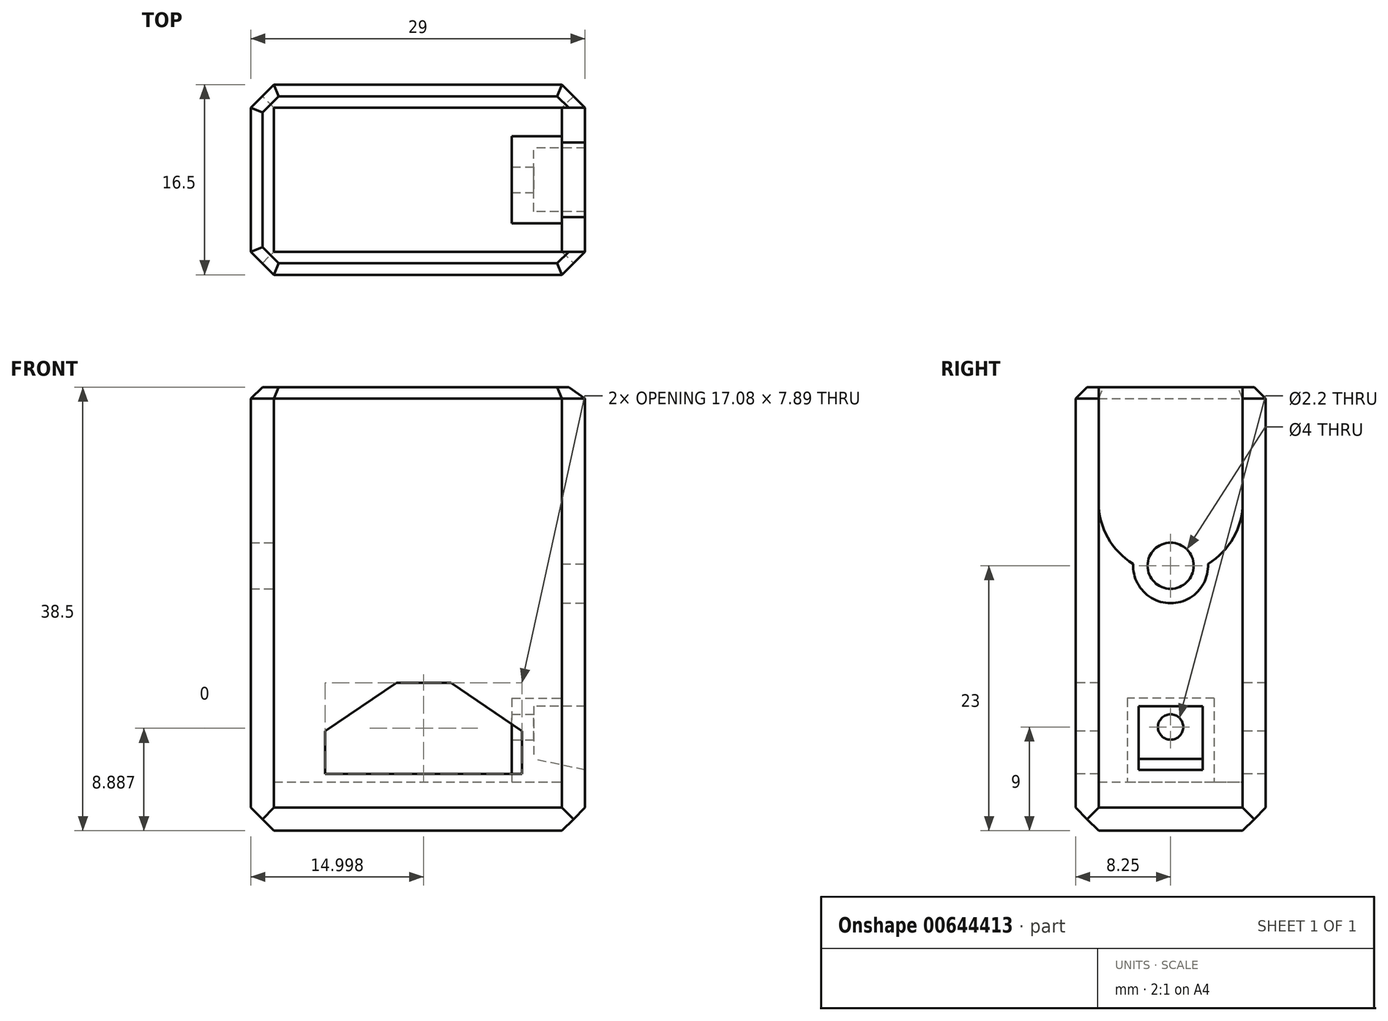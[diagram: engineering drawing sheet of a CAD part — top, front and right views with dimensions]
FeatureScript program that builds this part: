
annotation { "Feature Type Name" : "Feature", "Feature Type Description" : "" }
export const myFeature = defineFeature(function(context is Context, id is Id, definition is map)
    precondition{}
    {
        {
            var Q0;
            Q0=qCreatedBy(makeId("Top.planeOp"),FACE);
            var sketch = newSketch(context, id + "F0", { "sketchPlane" : qUnion([Q0])});
            skLineSegment(sketch, "E0.bottom", {"start": v(0, 0) * mm, "end": v(29, 0) * mm});
            skLineSegment(sketch, "E0.top", {"start": v(0, 16.5) * mm, "end": v(29, 16.5) * mm});
            skLineSegment(sketch, "E0.left", {"start": v(0, 0) * mm, "end": v(0, 16.5) * mm});
            skLineSegment(sketch, "E0.right", {"start": v(29, 0) * mm, "end": v(29, 16.5) * mm});
            skSolve(sketch);
        }
        {
            var Q0;
            Q0 = qSketchRegion(id + "F0", true);
            extrude(context, id + "F1", {"entities" : qUnion([Q0]), "depth" : 38.5 * mm, "offsetDistance" : 25 * mm});
        }
        {
            var Q0;
            Q0=makeQuery(id+"F1.opExtrude","CAP_FACE",FACE,{"disambiguationData":[OSD([sQuery(id+"F0.wireOp",EDGE,"E0.bottom"),sQuery(id+"F0.wireOp",EDGE,"E0.top"),sQuery(id+"F0.wireOp",EDGE,"E0.left"),sQuery(id+"F0.wireOp",EDGE,"E0.right")])],"isStart":false});
            shell(context, id + "F2", {"entities" : qUnion([Q0]), "thickness" : 2 * mm});
        }
        {
            var Q0;
            Q0=makeQuery(id+"F2.opShell","OFFSET_FACE",FACE,{"disambiguationData":[OSD([sQuery(id+"F0.wireOp",EDGE,"E0.bottom"),sQuery(id+"F0.wireOp",EDGE,"E0.top"),sQuery(id+"F0.wireOp",EDGE,"E0.left"),sQuery(id+"F0.wireOp",EDGE,"E0.right")])]});
            extrude(context, id + "F3", {"entities" : qUnion([Q0]), "operationType" : NewBodyOperationType.ADD, "depth" : 2.25 * mm, "offsetDistance" : 25 * mm});
        }
        {
            var Q0;
            Q0=makeQuery(id+"F1.opExtrude","SWEPT_EDGE",EDGE,{"disambiguationData":[OSD([sQuery(id+"F0.wireOp",EDGE,"E0.top"),sQuery(id+"F0.wireOp",EDGE,"E0.right")])]});
            var Q1;
            Q1=makeQuery(id+"F1.opExtrude","SWEPT_EDGE",EDGE,{"disambiguationData":[OSD([sQuery(id+"F0.wireOp",EDGE,"E0.top"),sQuery(id+"F0.wireOp",EDGE,"E0.left")])]});
            var Q2;
            Q2=makeQuery(id+"F1.opExtrude","SWEPT_EDGE",EDGE,{"disambiguationData":[OSD([sQuery(id+"F0.wireOp",EDGE,"E0.bottom"),sQuery(id+"F0.wireOp",EDGE,"E0.left")])]});
            var Q3;
            Q3=makeQuery(id+"F1.opExtrude","SWEPT_EDGE",EDGE,{"disambiguationData":[OSD([sQuery(id+"F0.wireOp",EDGE,"E0.bottom"),sQuery(id+"F0.wireOp",EDGE,"E0.right")])]});
            chamfer(context, id + "F4", {"entities" : qUnion([Q0, Q1, Q2, Q3]), "width" : 2 * mm, "tangentPropagation" : true});
        }
        {
            var Q0;
            Q0=makeQuery(id+"F1.opExtrude","CAP_EDGE",EDGE,{"disambiguationData":[OSD([sQuery(id+"F0.wireOp",EDGE,"E0.left")])],"isStart":true});
            var Q1;
            Q1=makeQuery(id+"F1.opExtrude","CAP_EDGE",EDGE,{"disambiguationData":[OSD([sQuery(id+"F0.wireOp",EDGE,"E0.bottom")])],"isStart":true});
            var Q2;
            Q2=makeQuery(id+"F1.opExtrude","CAP_EDGE",EDGE,{"disambiguationData":[OSD([sQuery(id+"F0.wireOp",EDGE,"E0.right")])],"isStart":true});
            var Q3;
            Q3=makeQuery(id+"F1.opExtrude","CAP_EDGE",EDGE,{"disambiguationData":[OSD([sQuery(id+"F0.wireOp",EDGE,"E0.top")])],"isStart":true});
            chamfer(context, id + "F5", {"entities" : qUnion([Q0, Q1, Q2, Q3]), "width" : 2 * mm, "tangentPropagation" : true});
        }
        {
            var Q0;
            Q0=makeQuery(id+"F1.opExtrude","CAP_EDGE",EDGE,{"disambiguationData":[OSD([sQuery(id+"F0.wireOp",EDGE,"E0.top")])],"isStart":false});
            var Q1;
            Q1=makeQuery(id+"F1.opExtrude","CAP_EDGE",EDGE,{"disambiguationData":[OSD([sQuery(id+"F0.wireOp",EDGE,"E0.right")])],"isStart":false});
            var Q2;
            Q2=makeQuery(id+"F1.opExtrude","CAP_EDGE",EDGE,{"disambiguationData":[OSD([sQuery(id+"F0.wireOp",EDGE,"E0.bottom")])],"isStart":false});
            var Q3;
            Q3=makeQuery(id+"F1.opExtrude","CAP_EDGE",EDGE,{"disambiguationData":[OSD([sQuery(id+"F0.wireOp",EDGE,"E0.left")])],"isStart":false});
            var Q4;
            {var subQ0=sQuery(id+"F0.wireOp",EDGE,"E0.left");var subQ1=sQuery(id+"F0.wireOp",EDGE,"E0.top");Q4=makeQuery(id+"F4.opChamfer","BLEND_EDGE",EDGE,{"blendedFrom":[makeQuery(id+"F1.opExtrude","SWEPT_EDGE",EDGE,{"disambiguationData":[OSD([subQ1,subQ0])]}),makeQuery(id+"F1.opExtrude","CAP_FACE",FACE,{"disambiguationData":[OSD([sQuery(id+"F0.wireOp",EDGE,"E0.bottom"),subQ1,subQ0,sQuery(id+"F0.wireOp",EDGE,"E0.right")])],"isStart":false})],"blendedInto":[makeQuery(id+"F1.opExtrude","CAP_FACE",FACE,{"disambiguationData":[OSD([sQuery(id+"F0.wireOp",EDGE,"E0.bottom"),subQ1,subQ0,sQuery(id+"F0.wireOp",EDGE,"E0.right")])],"isStart":false})]});}
            var Q5;
            {var subQ0=sQuery(id+"F0.wireOp",EDGE,"E0.right");var subQ1=sQuery(id+"F0.wireOp",EDGE,"E0.top");Q5=makeQuery(id+"F4.opChamfer","BLEND_EDGE",EDGE,{"blendedFrom":[makeQuery(id+"F1.opExtrude","SWEPT_EDGE",EDGE,{"disambiguationData":[OSD([subQ1,subQ0])]}),makeQuery(id+"F1.opExtrude","CAP_FACE",FACE,{"disambiguationData":[OSD([sQuery(id+"F0.wireOp",EDGE,"E0.bottom"),subQ1,sQuery(id+"F0.wireOp",EDGE,"E0.left"),subQ0])],"isStart":false})],"blendedInto":[makeQuery(id+"F1.opExtrude","CAP_FACE",FACE,{"disambiguationData":[OSD([sQuery(id+"F0.wireOp",EDGE,"E0.bottom"),subQ1,sQuery(id+"F0.wireOp",EDGE,"E0.left"),subQ0])],"isStart":false})]});}
            var Q6;
            {var subQ0=sQuery(id+"F0.wireOp",EDGE,"E0.right");var subQ1=sQuery(id+"F0.wireOp",EDGE,"E0.bottom");Q6=makeQuery(id+"F4.opChamfer","BLEND_EDGE",EDGE,{"blendedFrom":[makeQuery(id+"F1.opExtrude","SWEPT_EDGE",EDGE,{"disambiguationData":[OSD([subQ1,subQ0])]}),makeQuery(id+"F1.opExtrude","CAP_FACE",FACE,{"disambiguationData":[OSD([subQ1,sQuery(id+"F0.wireOp",EDGE,"E0.top"),sQuery(id+"F0.wireOp",EDGE,"E0.left"),subQ0])],"isStart":false})],"blendedInto":[makeQuery(id+"F1.opExtrude","CAP_FACE",FACE,{"disambiguationData":[OSD([subQ1,sQuery(id+"F0.wireOp",EDGE,"E0.top"),sQuery(id+"F0.wireOp",EDGE,"E0.left"),subQ0])],"isStart":false})]});}
            var Q7;
            {var subQ0=sQuery(id+"F0.wireOp",EDGE,"E0.left");var subQ1=sQuery(id+"F0.wireOp",EDGE,"E0.bottom");Q7=makeQuery(id+"F4.opChamfer","BLEND_EDGE",EDGE,{"blendedFrom":[makeQuery(id+"F1.opExtrude","SWEPT_EDGE",EDGE,{"disambiguationData":[OSD([subQ1,subQ0])]}),makeQuery(id+"F1.opExtrude","CAP_FACE",FACE,{"disambiguationData":[OSD([subQ1,sQuery(id+"F0.wireOp",EDGE,"E0.top"),subQ0,sQuery(id+"F0.wireOp",EDGE,"E0.right")])],"isStart":false})],"blendedInto":[makeQuery(id+"F1.opExtrude","CAP_FACE",FACE,{"disambiguationData":[OSD([subQ1,sQuery(id+"F0.wireOp",EDGE,"E0.top"),subQ0,sQuery(id+"F0.wireOp",EDGE,"E0.right")])],"isStart":false})]});}
            chamfer(context, id + "F6", {"entities" : qUnion([Q0, Q1, Q2, Q3, Q4, Q5, Q6, Q7]), "width" : 1 * mm, "tangentPropagation" : true});
        }
        {
            var Q0;
            Q0=makeQuery(id+"F1.opExtrude","SWEPT_FACE",FACE,{"disambiguationData":[OSD([sQuery(id+"F0.wireOp",EDGE,"E0.bottom")])]});
            var sketch = newSketch(context, id + "F7", { "sketchPlane" : qUnion([Q0])});
            skLineSegment(sketch, "E1", {"start": v(12.63, 12.83) * mm, "end": v(6.46, 8.66) * mm});
            skLineSegment(sketch, "E2", {"start": v(6.46, 4.94) * mm, "end": v(23.54, 4.94) * mm});
            skLineSegment(sketch, "E3", {"start": v(23.54, 4.94) * mm, "end": v(23.54, 8.66) * mm});
            skLineSegment(sketch, "E4", {"start": v(23.54, 8.66) * mm, "end": v(17.36, 12.83) * mm});
            skLineSegment(sketch, "E5", {"start": v(17.36, 12.83) * mm, "end": v(12.63, 12.83) * mm});
            skLineSegment(sketch, "E6", {"start": v(6.46, 8.66) * mm, "end": v(6.46, 4.94) * mm});
            skSolve(sketch);
        }
        {
            var Q0;
            Q0=makeQuery(id+"F7.imprint","IMPRINT",FACE,{"disambiguationData":[TD([[makeQuery(id+"F7.imprint","IMPRINT",EDGE,{"derivedFrom":sQuery(id+"F7.wireOp",EDGE,"E1")}),1.0]])]});
            extrude(context, id + "F8", {"entities" : qUnion([Q0]), "operationType" : NewBodyOperationType.REMOVE, "endBound" : BoundingType.THROUGH_ALL, "oppositeDirection" : true, "depth" : 25 * mm, "offsetDistance" : 25 * mm});
        }
        {
            var Q0;
            Q0=makeQuery(id+"F1.opExtrude","SWEPT_FACE",FACE,{"disambiguationData":[OSD([sQuery(id+"F0.wireOp",EDGE,"E0.right")])]});
            var sketch = newSketch(context, id + "F9", { "sketchPlane" : qUnion([Q0])});
            skCircle(sketch, "E7", {"center": v(8.25, 23) * mm, "radius": 3.25 * mm});
            skCircle(sketch, "E8", {"center": v(8.25, 28.5) * mm, "radius": 6.25 * mm});
            skLineSegment(sketch, "E9.bottom", {"start": v(2, 38.5) * mm, "end": v(14.5, 38.5) * mm});
            skLineSegment(sketch, "E9.top", {"start": v(2, 28.5) * mm, "end": v(14.5, 28.5) * mm});
            skLineSegment(sketch, "E9.left", {"start": v(2, 38.5) * mm, "end": v(2, 28.5) * mm});
            skLineSegment(sketch, "E9.right", {"start": v(14.5, 38.5) * mm, "end": v(14.5, 28.5) * mm});
            skSolve(sketch);
        }
        {
            var Q0;
            Q0 = qSketchRegion(id + "F9", true);
            extrude(context, id + "F10", {"entities" : qUnion([Q0]), "operationType" : NewBodyOperationType.REMOVE, "endBound" : BoundingType.UP_TO_NEXT, "oppositeDirection" : true, "depth" : 25 * mm, "offsetDistance" : 25 * mm});
        }
        {
            var Q0;
            Q0=makeQuery(id+"F2.opShell","OFFSET_FACE",FACE,{"disambiguationData":[OSD([sQuery(id+"F0.wireOp",EDGE,"E0.left")])]});
            var sketch = newSketch(context, id + "F11", { "sketchPlane" : qUnion([Q0])});
            skCircle(sketch, "E10", {"center": v(8.25, 23) * mm, "radius": 2 * mm});
            skSolve(sketch);
        }
        {
            var Q0;
            Q0 = qSketchRegion(id + "F11", true);
            extrude(context, id + "F12", {"entities" : qUnion([Q0]), "operationType" : NewBodyOperationType.REMOVE, "endBound" : BoundingType.THROUGH_ALL, "oppositeDirection" : true, "depth" : 25 * mm, "offsetDistance" : 25 * mm});
        }
        {
            var Q0;
            Q0=makeQuery(id+"F2.opShell","OFFSET_FACE",FACE,{"disambiguationData":[OSD([sQuery(id+"F0.wireOp",EDGE,"E0.right")])]});
            var sketch = newSketch(context, id + "F13", { "sketchPlane" : qUnion([Q0])});
            skLineSegment(sketch, "E11.bottom", {"start": v(-12.02, 11.5) * mm, "end": v(-4.48, 11.5) * mm});
            skLineSegment(sketch, "E11.top", {"start": v(-12.02, 4.25) * mm, "end": v(-4.48, 4.25) * mm});
            skLineSegment(sketch, "E11.left", {"start": v(-12.02, 11.5) * mm, "end": v(-12.02, 4.25) * mm});
            skLineSegment(sketch, "E11.right", {"start": v(-4.48, 11.5) * mm, "end": v(-4.48, 4.25) * mm});
            skCircle(sketch, "E12", {"center": v(-8.25, 9) * mm, "radius": 1.1 * mm});
            skSolve(sketch);
        }
        {
            var Q0;
            Q0 = qSketchRegion(id + "F13", true);
            extrude(context, id + "F14", {"entities" : qUnion([Q0]), "operationType" : NewBodyOperationType.ADD, "depth" : 4.35 * mm, "offsetDistance" : 25 * mm});
        }
        {
            var Q0;
            Q0=makeQuery(id+"F1.opExtrude","SWEPT_FACE",FACE,{"disambiguationData":[OSD([sQuery(id+"F0.wireOp",EDGE,"E0.right")])]});
            var sketch = newSketch(context, id + "F15", { "sketchPlane" : qUnion([Q0])});
            skLineSegment(sketch, "E13.bottom", {"start": v(5.48, 10.8) * mm, "end": v(11.02, 10.8) * mm});
            skLineSegment(sketch, "E13.top", {"start": v(5.48, 5.27) * mm, "end": v(11.02, 5.27) * mm});
            skLineSegment(sketch, "E13.left", {"start": v(5.48, 10.8) * mm, "end": v(5.48, 5.27) * mm});
            skLineSegment(sketch, "E13.right", {"start": v(11.02, 10.8) * mm, "end": v(11.02, 5.27) * mm});
            skSolve(sketch);
        }
        {
            var Q0;
            Q0=makeQuery(id+"F15.imprint","IMPRINT",FACE,{"disambiguationData":[TD([[makeQuery(id+"F15.imprint","IMPRINT",EDGE,{"derivedFrom":sQuery(id+"F15.wireOp",EDGE,"E13.bottom")}),1.0]])]});
            cPlane(context, id + "F16", {"entities" : qUnion([Q0]), "cplaneType" : CPlaneType.OFFSET, "offset" : 4.45 * mm, "oppositeDirection" : true, "width" : 150 * mm, "height" : 150 * mm});
        }
        {
            var Q0;
            Q0=qCreatedBy(id+"F16.planeOp",FACE);
            var sketch = newSketch(context, id + "F17", { "sketchPlane" : qUnion([Q0])});
            skLineSegment(sketch, "E14.bottom", {"start": v(5.48, 10.8) * mm, "end": v(11.02, 10.8) * mm});
            skLineSegment(sketch, "E14.top", {"start": v(5.48, 6.22) * mm, "end": v(11.02, 6.22) * mm});
            skLineSegment(sketch, "E14.left", {"start": v(5.48, 10.8) * mm, "end": v(5.48, 6.22) * mm});
            skLineSegment(sketch, "E14.right", {"start": v(11.02, 10.8) * mm, "end": v(11.02, 6.22) * mm});
            skSolve(sketch);
        }
        {
            var Q1;
            Q1 = qSketchRegion(id + "F15", true);
            var Q2;
            Q2 = qSketchRegion(id + "F17", true);
            loft(context, id + "F18", {"operationType" : NewBodyOperationType.REMOVE, "sheetProfilesArray" : [{ "sheetProfileEntities" : qUnion([Q1]) }, { "sheetProfileEntities" : qUnion([Q2]) }]});
        }
    });
